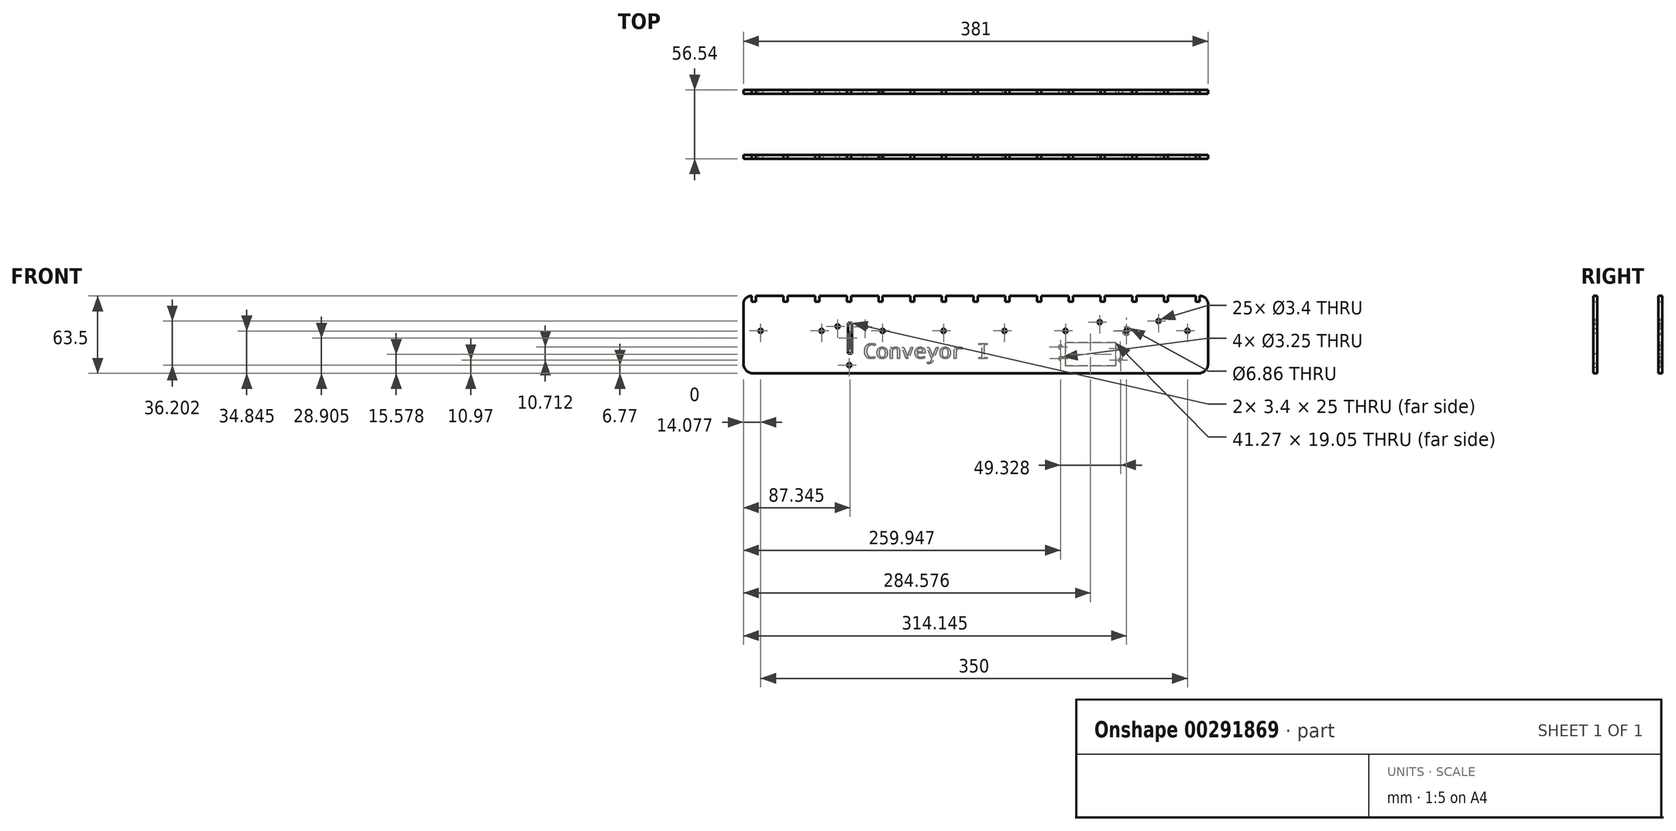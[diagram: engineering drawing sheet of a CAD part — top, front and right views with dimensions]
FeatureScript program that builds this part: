
annotation { "Feature Type Name" : "Feature", "Feature Type Description" : "" }
export const myFeature = defineFeature(function(context is Context, id is Id, definition is map)
    precondition{}
    {
        {
            var Q0;
            Q0=qCreatedBy(makeId("Front.planeOp"),FACE);
            var sketch = newSketch(context, id + "F0", { "sketchPlane" : qUnion([Q0])});
            skLineSegment(sketch, "E0.bottom", {"start": v(-187.07, 64.33) * mm, "end": v(181.23, 64.33) * mm});
            skLineSegment(sketch, "E0.top", {"start": v(-185.42, 0.83) * mm, "end": v(179.58, 0.83) * mm});
            skLineSegment(sketch, "E0.left", {"start": v(-193.42, 57.98) * mm, "end": v(-193.42, 8.83) * mm});
            skLineSegment(sketch, "E0.right", {"start": v(187.58, 57.98) * mm, "end": v(187.58, 8.83) * mm});
            skPoint(sketch, "E1.visualSharp", {"position": v(-193.42, 64.33) * mm});
            skArc(sketch, "E1.filletArc", {"start": v(-187.07, 64.33) * mm, "mid": v(-191.56, 62.47) * mm, "end": v(-193.42, 57.98) * mm});
            skPoint(sketch, "E2.visualSharp", {"position": v(187.58, 64.33) * mm});
            skArc(sketch, "E2.filletArc", {"start": v(187.58, 57.98) * mm, "mid": v(185.72, 62.47) * mm, "end": v(181.23, 64.33) * mm});
            skPoint(sketch, "E3.visualSharp", {"position": v(-193.42, 0.83) * mm});
            skArc(sketch, "E3.filletArc", {"start": v(-193.42, 8.83) * mm, "mid": v(-191.07, 3.17) * mm, "end": v(-185.42, 0.83) * mm});
            skPoint(sketch, "E4.visualSharp", {"position": v(187.58, 0.83) * mm});
            skArc(sketch, "E4.filletArc", {"start": v(179.58, 0.83) * mm, "mid": v(185.24, 3.17) * mm, "end": v(187.58, 8.83) * mm});
            skSolve(sketch);
        }
        {
            var Q0;
            {var subQ1=sQuery(id+"F0.wireOp",EDGE,"E0.top");Q0=makeQuery(id+"F0.imprint","IMPRINT",FACE,{"disambiguationData":[TD([[makeQuery(id+"F0.imprint","IMPRINT",EDGE,{"derivedFrom":subQ1}),1.0]])]});}
            var Q1;
            {var subQ0=sQuery(id+"F0.wireOp",EDGE,"E0.left");var subQ1=sQuery(id+"F0.wireOp",EDGE,"E0.bottom");var subQ2=makeQuery(id+"F0.imprint","INTERSECT",VERTEX,{"derivedFrom":[subQ1,subQ0]});Q1=makeQuery(id+"F0.imprint","IMPRINT",FACE,{"disambiguationData":[TD([[makeQuery(id+"F0.imprint","IMPRINT",EDGE,{"disambiguationData":[TD([[subQ2,-1.0]])],"derivedFrom":subQ1}),-1.0]])]});}
            var Q2;
            {var subQ0=sQuery(id+"F0.wireOp",EDGE,"tyeUReP9-LIIo-t7GG-6YUm-Q0LLwcb4cyRe");var subQ1=sQuery(id+"F0.wireOp",EDGE,"E0.right");var subQ3=makeQuery(id+"F0.imprint","INTERSECT",VERTEX,{"derivedFrom":[subQ1,subQ0]});Q2=makeQuery(id+"F0.imprint","IMPRINT",FACE,{"disambiguationData":[TD([[makeQuery(id+"F0.imprint","IMPRINT",EDGE,{"disambiguationData":[TD([[subQ3,1.0]])],"derivedFrom":subQ1}),1.0]])]});}
            var Q3;
            {var subQ0=sQuery(id+"F0.wireOp",EDGE,"E0.left");var subQ1=sQuery(id+"F0.wireOp",EDGE,"E0.bottom");var subQ2=makeQuery(id+"F0.imprint","INTERSECT",VERTEX,{"derivedFrom":[subQ1,subQ0]});Q3=makeQuery(id+"F0.imprint","IMPRINT",FACE,{"disambiguationData":[TD([[makeQuery(id+"F0.imprint","IMPRINT",EDGE,{"disambiguationData":[TD([[subQ2,-1.0]])],"derivedFrom":subQ1}),1.0]])]});}
            var Q4;
            {var subQ0=sQuery(id+"F0.wireOp",EDGE,"tyeUReP9-LIIo-t7GG-6YUm-Q0LLwcb4cyRe");var subQ1=sQuery(id+"F0.wireOp",EDGE,"E0.right");var subQ3=makeQuery(id+"F0.imprint","INTERSECT",VERTEX,{"derivedFrom":[subQ1,subQ0]});Q4=makeQuery(id+"F0.imprint","IMPRINT",FACE,{"disambiguationData":[TD([[makeQuery(id+"F0.imprint","IMPRINT",EDGE,{"disambiguationData":[TD([[subQ3,1.0]])],"derivedFrom":subQ1}),-1.0]])]});}
            extrude(context, id + "F1", {"entities" : qUnion([Q0, Q1, Q2, Q3, Q4]), "depth" : 3.2 * mm});
        }
        {
            var Q0;
            Q0=qCreatedBy(makeId("Front.planeOp"),FACE);
            var sketch = newSketch(context, id + "F2", { "sketchPlane" : qUnion([Q0])});
            skLineSegment(sketch, "E5.bottom", {"start": v(-186.65, 64.86) * mm, "end": v(-183.25, 64.86) * mm});
            skLineSegment(sketch, "E5.top", {"start": v(-186.65, 59.86) * mm, "end": v(-183.25, 59.86) * mm});
            skLineSegment(sketch, "E5.left", {"start": v(-186.65, 64.86) * mm, "end": v(-186.65, 59.86) * mm});
            skLineSegment(sketch, "E5.right", {"start": v(-183.25, 64.86) * mm, "end": v(-183.25, 59.86) * mm});
            skLineSegment(sketch, "E6.1.0.0", {"start": v(-160.65, 59.86) * mm, "end": v(-157.25, 59.86) * mm});
            skLineSegment(sketch, "E6.1.0.1", {"start": v(-160.65, 64.86) * mm, "end": v(-160.65, 59.86) * mm});
            skLineSegment(sketch, "E6.1.0.2", {"start": v(-157.25, 64.86) * mm, "end": v(-157.25, 59.86) * mm});
            skLineSegment(sketch, "E6.1.0.3", {"start": v(-160.65, 64.86) * mm, "end": v(-157.25, 64.86) * mm});
            skLineSegment(sketch, "E6.2.0.0", {"start": v(-134.65, 59.86) * mm, "end": v(-131.25, 59.86) * mm});
            skLineSegment(sketch, "E6.2.0.1", {"start": v(-134.65, 64.86) * mm, "end": v(-134.65, 59.86) * mm});
            skLineSegment(sketch, "E6.2.0.2", {"start": v(-131.25, 64.86) * mm, "end": v(-131.25, 59.86) * mm});
            skLineSegment(sketch, "E6.2.0.3", {"start": v(-134.65, 64.86) * mm, "end": v(-131.25, 64.86) * mm});
            skLineSegment(sketch, "E6.3.0.0", {"start": v(-108.65, 59.86) * mm, "end": v(-105.25, 59.86) * mm});
            skLineSegment(sketch, "E6.3.0.1", {"start": v(-108.65, 64.86) * mm, "end": v(-108.65, 59.86) * mm});
            skLineSegment(sketch, "E6.3.0.2", {"start": v(-105.25, 64.86) * mm, "end": v(-105.25, 59.86) * mm});
            skLineSegment(sketch, "E6.3.0.3", {"start": v(-108.65, 64.86) * mm, "end": v(-105.25, 64.86) * mm});
            skLineSegment(sketch, "E6.4.0.0", {"start": v(-82.65, 59.86) * mm, "end": v(-79.25, 59.86) * mm});
            skLineSegment(sketch, "E6.4.0.1", {"start": v(-82.65, 64.86) * mm, "end": v(-82.65, 59.86) * mm});
            skLineSegment(sketch, "E6.4.0.2", {"start": v(-79.25, 64.86) * mm, "end": v(-79.25, 59.86) * mm});
            skLineSegment(sketch, "E6.4.0.3", {"start": v(-82.65, 64.86) * mm, "end": v(-79.25, 64.86) * mm});
            skLineSegment(sketch, "E6.5.0.0", {"start": v(-56.65, 59.86) * mm, "end": v(-53.25, 59.86) * mm});
            skLineSegment(sketch, "E6.5.0.1", {"start": v(-56.65, 64.86) * mm, "end": v(-56.65, 59.86) * mm});
            skLineSegment(sketch, "E6.5.0.2", {"start": v(-53.25, 64.86) * mm, "end": v(-53.25, 59.86) * mm});
            skLineSegment(sketch, "E6.5.0.3", {"start": v(-56.65, 64.86) * mm, "end": v(-53.25, 64.86) * mm});
            skLineSegment(sketch, "E6.6.0.0", {"start": v(-30.65, 59.86) * mm, "end": v(-27.25, 59.86) * mm});
            skLineSegment(sketch, "E6.6.0.1", {"start": v(-30.65, 64.86) * mm, "end": v(-30.65, 59.86) * mm});
            skLineSegment(sketch, "E6.6.0.2", {"start": v(-27.25, 64.86) * mm, "end": v(-27.25, 59.86) * mm});
            skLineSegment(sketch, "E6.6.0.3", {"start": v(-30.65, 64.86) * mm, "end": v(-27.25, 64.86) * mm});
            skLineSegment(sketch, "E6.7.0.0", {"start": v(-4.65, 59.86) * mm, "end": v(-1.25, 59.86) * mm});
            skLineSegment(sketch, "E6.7.0.1", {"start": v(-4.65, 64.86) * mm, "end": v(-4.65, 59.86) * mm});
            skLineSegment(sketch, "E6.7.0.2", {"start": v(-1.25, 64.86) * mm, "end": v(-1.25, 59.86) * mm});
            skLineSegment(sketch, "E6.7.0.3", {"start": v(-4.65, 64.86) * mm, "end": v(-1.25, 64.86) * mm});
            skLineSegment(sketch, "E6.8.0.0", {"start": v(21.35, 59.86) * mm, "end": v(24.75, 59.86) * mm});
            skLineSegment(sketch, "E6.8.0.1", {"start": v(21.35, 64.86) * mm, "end": v(21.35, 59.86) * mm});
            skLineSegment(sketch, "E6.8.0.2", {"start": v(24.75, 64.86) * mm, "end": v(24.75, 59.86) * mm});
            skLineSegment(sketch, "E6.8.0.3", {"start": v(21.35, 64.86) * mm, "end": v(24.75, 64.86) * mm});
            skLineSegment(sketch, "E6.9.0.0", {"start": v(47.35, 59.86) * mm, "end": v(50.75, 59.86) * mm});
            skLineSegment(sketch, "E6.9.0.1", {"start": v(47.35, 64.86) * mm, "end": v(47.35, 59.86) * mm});
            skLineSegment(sketch, "E6.9.0.2", {"start": v(50.75, 64.86) * mm, "end": v(50.75, 59.86) * mm});
            skLineSegment(sketch, "E6.9.0.3", {"start": v(47.35, 64.86) * mm, "end": v(50.75, 64.86) * mm});
            skLineSegment(sketch, "E6.10.0.0", {"start": v(73.35, 59.86) * mm, "end": v(76.75, 59.86) * mm});
            skLineSegment(sketch, "E6.10.0.1", {"start": v(73.35, 64.86) * mm, "end": v(73.35, 59.86) * mm});
            skLineSegment(sketch, "E6.10.0.2", {"start": v(76.75, 64.86) * mm, "end": v(76.75, 59.86) * mm});
            skLineSegment(sketch, "E6.10.0.3", {"start": v(73.35, 64.86) * mm, "end": v(76.75, 64.86) * mm});
            skLineSegment(sketch, "E6.11.0.0", {"start": v(99.35, 59.86) * mm, "end": v(102.75, 59.86) * mm});
            skLineSegment(sketch, "E6.11.0.1", {"start": v(99.35, 64.86) * mm, "end": v(99.35, 59.86) * mm});
            skLineSegment(sketch, "E6.11.0.2", {"start": v(102.75, 64.86) * mm, "end": v(102.75, 59.86) * mm});
            skLineSegment(sketch, "E6.11.0.3", {"start": v(99.35, 64.86) * mm, "end": v(102.75, 64.86) * mm});
            skLineSegment(sketch, "E6.12.0.0", {"start": v(125.35, 59.86) * mm, "end": v(128.75, 59.86) * mm});
            skLineSegment(sketch, "E6.12.0.1", {"start": v(125.35, 64.86) * mm, "end": v(125.35, 59.86) * mm});
            skLineSegment(sketch, "E6.12.0.2", {"start": v(128.75, 64.86) * mm, "end": v(128.75, 59.86) * mm});
            skLineSegment(sketch, "E6.12.0.3", {"start": v(125.35, 64.86) * mm, "end": v(128.75, 64.86) * mm});
            skLineSegment(sketch, "E6.13.0.0", {"start": v(151.35, 59.86) * mm, "end": v(154.75, 59.86) * mm});
            skLineSegment(sketch, "E6.13.0.1", {"start": v(151.35, 64.86) * mm, "end": v(151.35, 59.86) * mm});
            skLineSegment(sketch, "E6.13.0.2", {"start": v(154.75, 64.86) * mm, "end": v(154.75, 59.86) * mm});
            skLineSegment(sketch, "E6.13.0.3", {"start": v(151.35, 64.86) * mm, "end": v(154.75, 64.86) * mm});
            skLineSegment(sketch, "E6.14.0.0", {"start": v(177.35, 59.86) * mm, "end": v(180.75, 59.86) * mm});
            skLineSegment(sketch, "E6.14.0.1", {"start": v(177.35, 64.86) * mm, "end": v(177.35, 59.86) * mm});
            skLineSegment(sketch, "E6.14.0.2", {"start": v(180.75, 64.86) * mm, "end": v(180.75, 59.86) * mm});
            skLineSegment(sketch, "E6.14.0.3", {"start": v(177.35, 64.86) * mm, "end": v(180.75, 64.86) * mm});
            skLineSegment(sketch, "E6.direction1", {"start": v(-186.65, 59.86) * mm, "end": v(-160.65, 59.86) * mm, "construction": true});
            skSolve(sketch);
        }
        {
            var Q0;
            Q0=qCreatedBy(makeId("Front.planeOp"),FACE);
            var sketch = newSketch(context, id + "F3", { "sketchPlane" : qUnion([Q0])});
            skCircle(sketch, "E7", {"center": v(-179.34, 35.75) * mm, "radius": 1.7 * mm});
            skCircle(sketch, "E8.1.0.0", {"center": v(-129.34, 35.75) * mm, "radius": 1.7 * mm});
            skCircle(sketch, "E8.2.0.0", {"center": v(-79.34, 35.75) * mm, "radius": 1.7 * mm});
            skCircle(sketch, "E8.3.0.0", {"center": v(-29.34, 35.75) * mm, "radius": 1.7 * mm});
            skCircle(sketch, "E8.4.0.0", {"center": v(20.66, 35.75) * mm, "radius": 1.7 * mm});
            skCircle(sketch, "E8.5.0.0", {"center": v(70.66, 35.75) * mm, "radius": 1.7 * mm});
            skCircle(sketch, "E8.6.0.0", {"center": v(120.66, 35.75) * mm, "radius": 1.7 * mm});
            skCircle(sketch, "E8.7.0.0", {"center": v(170.66, 35.75) * mm, "radius": 1.7 * mm});
            skLineSegment(sketch, "E8.direction1", {"start": v(-179.34, 35.75) * mm, "end": v(-129.34, 35.75) * mm, "construction": true});
            skSolve(sketch);
        }
        {
            var Q0;
            Q0 = qSketchRegion(id + "F2", true);
            extrude(context, id + "F4", {"entities" : qUnion([Q0]), "operationType" : NewBodyOperationType.REMOVE, "depth" : 25 * mm});
        }
        {
            var Q0;
            Q0 = qSketchRegion(id + "F3", true);
            extrude(context, id + "F5", {"entities" : qUnion([Q0]), "operationType" : NewBodyOperationType.REMOVE, "depth" : 25 * mm});
        }
        {
            var Q0;
            Q0=qCreatedBy(makeId("Front.planeOp"),FACE);
            var sketch = newSketch(context, id + "F6", { "sketchPlane" : qUnion([Q0])});
            skLineSegment(sketch, "E9.bottom", {"start": v(-107.78, 42.24) * mm, "end": v(-104.38, 42.24) * mm});
            skLineSegment(sketch, "E9.top", {"start": v(-107.78, 17.24) * mm, "end": v(-104.38, 17.24) * mm});
            skLineSegment(sketch, "E9.left", {"start": v(-107.78, 42.24) * mm, "end": v(-107.78, 17.24) * mm});
            skLineSegment(sketch, "E9.right", {"start": v(-104.38, 42.24) * mm, "end": v(-104.38, 17.24) * mm});
            skSolve(sketch);
        }
        {
            var Q0;
            Q0=qCreatedBy(makeId("Front.planeOp"),FACE);
            var sketch = newSketch(context, id + "F7", { "sketchPlane" : qUnion([Q0])});
            skCircle(sketch, "E10", {"center": v(-116.22, 39.44) * mm, "radius": 1.7 * mm});
            skCircle(sketch, "E11", {"center": v(-93.68, 39.16) * mm, "radius": 1.7 * mm});
            skCircle(sketch, "E12", {"center": v(98.67, 42.9) * mm, "radius": 1.7 * mm});
            skCircle(sketch, "E13", {"center": v(146.9, 43.8) * mm, "radius": 1.7 * mm});
            skCircle(sketch, "E14", {"center": v(-106.68, 7.6) * mm, "radius": 1.7 * mm});
            skSolve(sketch);
        }
        {
            var Q0;
            Q0 = qSketchRegion(id + "F6", true);
            extrude(context, id + "F8", {"entities" : qUnion([Q0]), "operationType" : NewBodyOperationType.REMOVE, "depth" : 25 * mm});
        }
        {
            var Q0;
            Q0=qCreatedBy(makeId("Front.planeOp"),FACE);
            var sketch = newSketch(context, id + "F9", { "sketchPlane" : qUnion([Q0])});
            skText(sketch, "E15", { "text": "Conveyor I", "fontName": "DroidSansMono.ttf"});
            const initialGuessF9  = {"E15": [-0.09508, 0.01308, 1, 0, 0.01239]};
            skSetInitialGuess(sketch, initialGuessF9);
            skSolve(sketch);
        }
        {
            var Q0;
            Q0 = qSketchRegion(id + "F7", true);
            extrude(context, id + "F10", {"entities" : qUnion([Q0]), "operationType" : NewBodyOperationType.REMOVE, "oppositeDirection" : true, "depth" : -5.08 * mm, "hasSecondDirection" : true, "secondDirectionOppositeDirection" : true, "secondDirectionDepth" : 63.5 * mm});
        }
        {
            var Q0;
            Q0=makeQuery(id+"F1.opExtrude","SWEPT_BODY",BODY,{"disambiguationData":[OSD([sQuery(id+"F0.wireOp",EDGE,"E0.bottom"),sQuery(id+"F0.wireOp",EDGE,"E0.top"),sQuery(id+"F0.wireOp",EDGE,"E0.left"),sQuery(id+"F0.wireOp",EDGE,"E0.right"),sQuery(id+"F0.wireOp",EDGE,"E1.filletArc"),sQuery(id+"F0.wireOp",EDGE,"E2.filletArc"),sQuery(id+"F0.wireOp",EDGE,"E3.filletArc"),sQuery(id+"F0.wireOp",EDGE,"E4.filletArc")])]});
            transform(context, id + "F11", {"entities" : qUnion([Q0]), "transformType" : TransformType.TRANSLATION_3D, "dx" : 0 * mm, "dy" : 53.34 * mm, "dz" : 0 * mm, "makeCopy" : true});
        }
        {
            var Q0;
            Q0 = qSketchRegion(id + "F9", true);
            extrude(context, id + "F12", {"entities" : qUnion([Q0]), "operationType" : NewBodyOperationType.REMOVE, "endBound" : BoundingType.SYMMETRIC, "oppositeDirection" : true, "depth" : 0.5 * mm});
        }
        {
            var Q0;
            Q0=qCreatedBy(makeId("Front.planeOp"),FACE);
            var sketch = newSketch(context, id + "F13", { "sketchPlane" : qUnion([Q0])});
            skCircle(sketch, "E16", {"center": v(120.72, 35.67) * mm, "radius": 3.43 * mm});
            skSolve(sketch);
        }
        {
            var Q0;
            Q0 = qSketchRegion(id + "F13", true);
            extrude(context, id + "F14", {"entities" : qUnion([Q0]), "operationType" : NewBodyOperationType.REMOVE, "oppositeDirection" : true, "depth" : 70 * mm});
        }
        {
            var Q0;
            Q0=qCreatedBy(makeId("Front.planeOp"),FACE);
            var sketch = newSketch(context, id + "F15", { "sketchPlane" : qUnion([Q0])});
            skLineSegment(sketch, "E17.bottom", {"start": v(111.8, 25.93) * mm, "end": v(70.52, 25.93) * mm});
            skLineSegment(sketch, "E17.top", {"start": v(111.8, 6.88) * mm, "end": v(70.52, 6.88) * mm});
            skLineSegment(sketch, "E17.left", {"start": v(111.8, 25.93) * mm, "end": v(111.8, 6.88) * mm});
            skLineSegment(sketch, "E17.right", {"start": v(70.52, 25.93) * mm, "end": v(70.52, 6.88) * mm});
            skSolve(sketch);
        }
        {
            var Q0;
            Q0=qCreatedBy(makeId("Front.planeOp"),FACE);
            var sketch = newSketch(context, id + "F16", { "sketchPlane" : qUnion([Q0])});
            skCircle(sketch, "E18", {"center": v(115.63, 21.29) * mm, "radius": 1.63 * mm});
            skCircle(sketch, "E19", {"center": v(115.86, 11.8) * mm, "radius": 1.63 * mm});
            skCircle(sketch, "E20", {"center": v(66.53, 22.51) * mm, "radius": 1.63 * mm});
            skCircle(sketch, "E21", {"center": v(66.75, 13.03) * mm, "radius": 1.63 * mm});
            skSolve(sketch);
        }
        {
            var Q0;
            Q0 = qSketchRegion(id + "F15", true);
            var Q1;
            Q1 = qSketchRegion(id + "F16", true);
            extrude(context, id + "F17", {"entities" : qUnion([Q0, Q1]), "operationType" : NewBodyOperationType.REMOVE, "oppositeDirection" : true, "depth" : 63.5 * mm});
        }
    });
